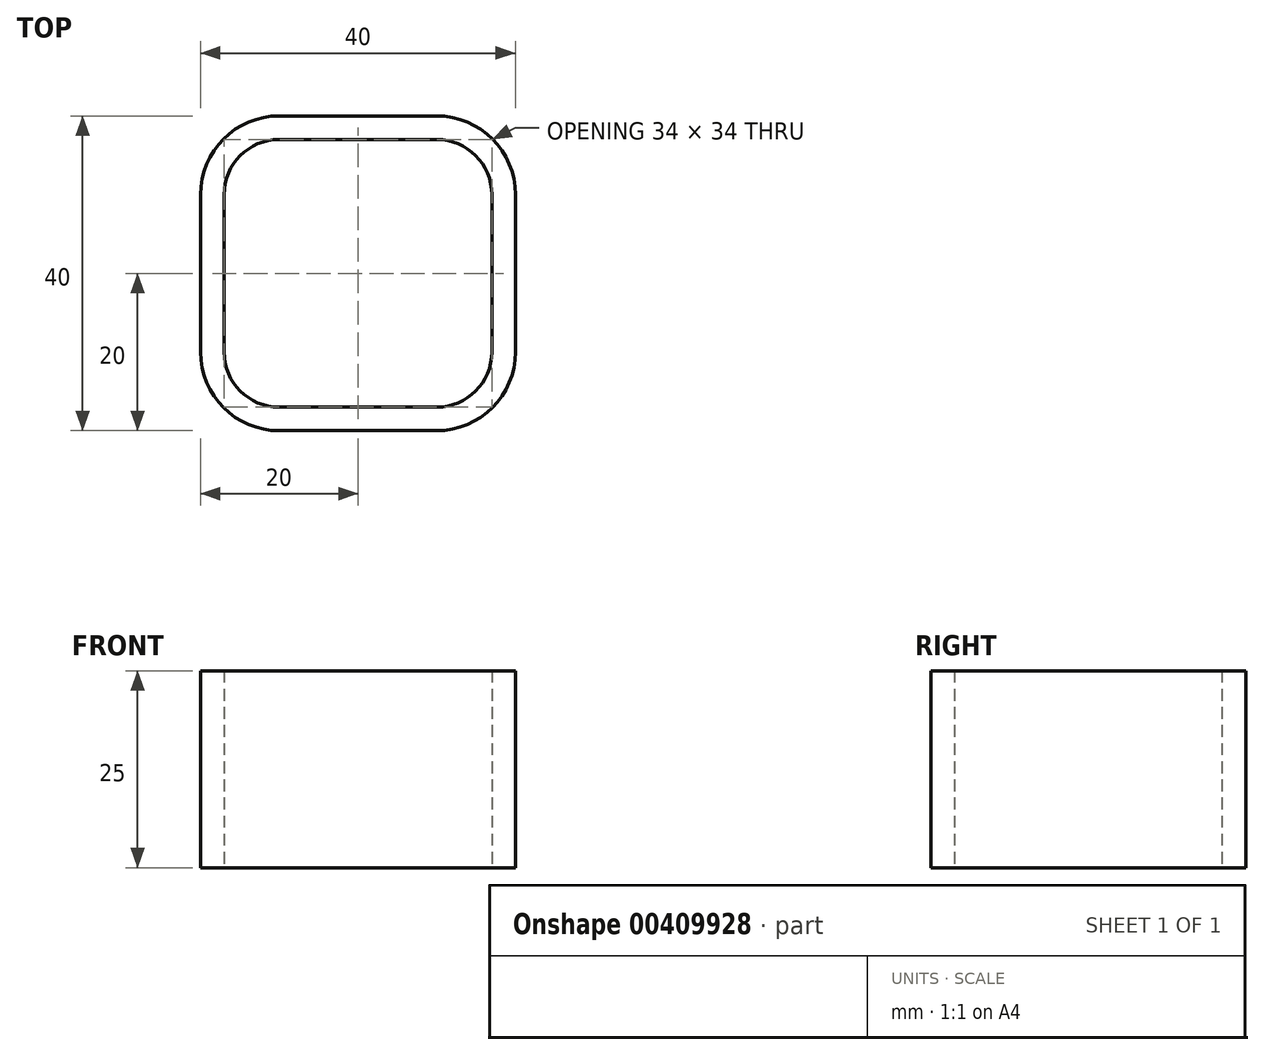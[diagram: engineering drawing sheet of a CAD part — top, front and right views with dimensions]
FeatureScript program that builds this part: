
annotation { "Feature Type Name" : "Feature", "Feature Type Description" : "" }
export const myFeature = defineFeature(function(context is Context, id is Id, definition is map)
    precondition{}
    {
        {
            var Q0;
            Q0=qCreatedBy(makeId("Top.planeOp"),FACE);
            var sketch = newSketch(context, id + "F0", { "sketchPlane" : qUnion([Q0])});
            skLineSegment(sketch, "E0.bottom", {"start": v(10, 20) * mm, "end": v(-10, 20) * mm});
            skLineSegment(sketch, "E0.top", {"start": v(10, -20) * mm, "end": v(-10, -20) * mm});
            skLineSegment(sketch, "E0.left", {"start": v(20, 10) * mm, "end": v(20, -10) * mm});
            skLineSegment(sketch, "E0.right", {"start": v(-20, 10) * mm, "end": v(-20, -10) * mm});
            skPoint(sketch, "E0.middle", {"position": v(0, 0) * mm});
            skPoint(sketch, "E1.visualSharp", {"position": v(-20, 20) * mm});
            skArc(sketch, "E1.filletArc", {"start": v(-10, 20) * mm, "mid": v(-17.07, 17.07) * mm, "end": v(-20, 10) * mm});
            skPoint(sketch, "E2.visualSharp", {"position": v(20, 20) * mm});
            skArc(sketch, "E2.filletArc", {"start": v(20, 10) * mm, "mid": v(17.07, 17.07) * mm, "end": v(10, 20) * mm});
            skPoint(sketch, "E3.visualSharp", {"position": v(20, -20) * mm});
            skArc(sketch, "E3.filletArc", {"start": v(10, -20) * mm, "mid": v(17.07, -17.07) * mm, "end": v(20, -10) * mm});
            skPoint(sketch, "E4.visualSharp", {"position": v(-20, -20) * mm});
            skArc(sketch, "E4.filletArc", {"start": v(-20, -10) * mm, "mid": v(-17.07, -17.07) * mm, "end": v(-10, -20) * mm});
            skLineSegment(sketch, "E5.bottom", {"start": v(10, 17) * mm, "end": v(-10, 17) * mm});
            skLineSegment(sketch, "E5.top", {"start": v(10, -17) * mm, "end": v(-10, -17) * mm});
            skLineSegment(sketch, "E5.left", {"start": v(17, 10) * mm, "end": v(17, -10) * mm});
            skLineSegment(sketch, "E5.right", {"start": v(-17, 10) * mm, "end": v(-17, -10) * mm});
            skPoint(sketch, "E6.visualSharp", {"position": v(-17, 17) * mm});
            skArc(sketch, "E6.filletArc", {"start": v(-10, 17) * mm, "mid": v(-14.95, 14.95) * mm, "end": v(-17, 10) * mm});
            skPoint(sketch, "E7.visualSharp", {"position": v(17, 17) * mm});
            skArc(sketch, "E7.filletArc", {"start": v(17, 10) * mm, "mid": v(14.95, 14.95) * mm, "end": v(10, 17) * mm});
            skPoint(sketch, "E8.visualSharp", {"position": v(17, -17) * mm});
            skArc(sketch, "E8.filletArc", {"start": v(10, -17) * mm, "mid": v(14.95, -14.95) * mm, "end": v(17, -10) * mm});
            skPoint(sketch, "E9.visualSharp", {"position": v(-17, -17) * mm});
            skArc(sketch, "E9.filletArc", {"start": v(-17, -10) * mm, "mid": v(-14.95, -14.95) * mm, "end": v(-10, -17) * mm});
            skSolve(sketch);
        }
        {
            var Q0;
            Q0=makeQuery(id+"F0.imprint","IMPRINT",FACE,{"disambiguationData":[TD([[makeQuery(id+"F0.imprint","IMPRINT",EDGE,{"derivedFrom":sQuery(id+"F0.wireOp",EDGE,"E0.bottom")}),1.0]])]});
            var sketch = newSketch(context, id + "F1", { "sketchPlane" : qUnion([Q0])});
            skSolve(sketch);
        }
        {
            var Q0;
            Q0 = qSketchRegion(id + "F1", true);
            var Q1;
            Q1=makeQuery(id+"F0.imprint","IMPRINT",FACE,{"disambiguationData":[TD([[makeQuery(id+"F0.imprint","IMPRINT",EDGE,{"derivedFrom":sQuery(id+"F0.wireOp",EDGE,"E0.bottom")}),1.0]])]});
            extrude(context, id + "F2", {"entities" : qUnion([Q0, Q1]), "depth" : 25 * mm});
        }
    });
